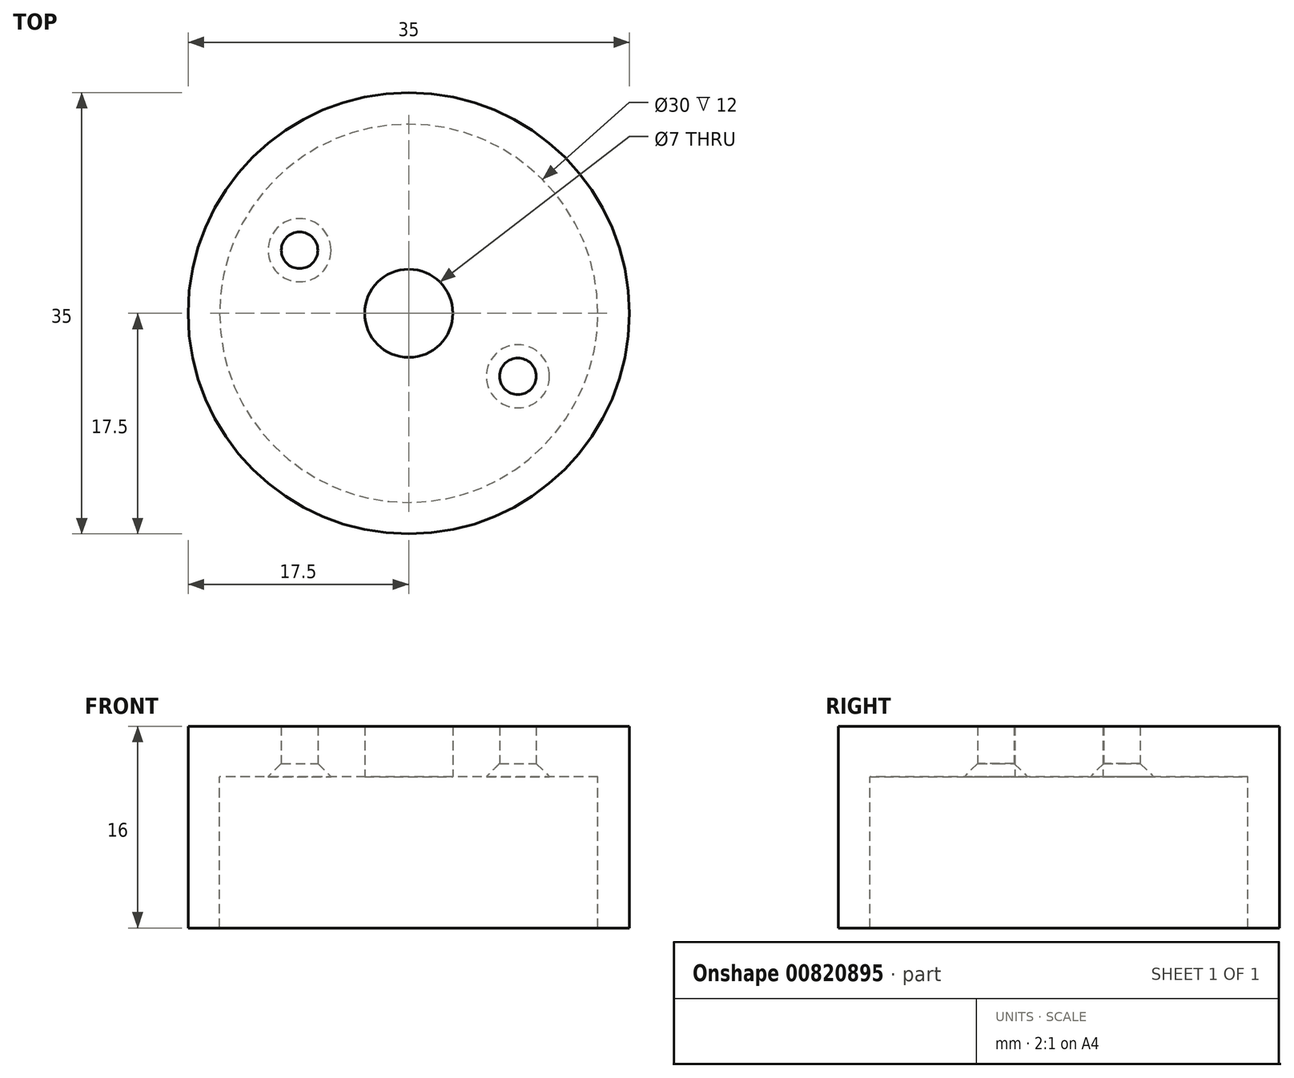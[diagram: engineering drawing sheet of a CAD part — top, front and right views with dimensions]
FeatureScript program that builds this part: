
annotation { "Feature Type Name" : "Feature", "Feature Type Description" : "" }
export const myFeature = defineFeature(function(context is Context, id is Id, definition is map)
    precondition{}
    {
        {
            var Q0;
            Q0=qCreatedBy(makeId("Top.planeOp"),FACE);
            var sketch = newSketch(context, id + "F0", { "sketchPlane" : qUnion([Q0])});
            skCircle(sketch, "E0", {"center": v(0, 0) * mm, "radius": 15 * mm});
            skPoint(sketch, "E1", {"position": v(-8.66, 5) * mm});
            skPoint(sketch, "E2.MirrorP", {"position": v(8.66, -5) * mm});
            skCircle(sketch, "E3", {"center": v(0, 0) * mm, "radius": 17.5 * mm});
            skSolve(sketch);
        }
        {
            var Q0;
            Q0=makeQuery(id+"F0.imprint","IMPRINT",FACE,{"disambiguationData":[TD([[makeQuery(id+"F0.imprint","IMPRINT",EDGE,{"derivedFrom":sQuery(id+"F0.wireOp",EDGE,"2a8dab0b-44af-4e55-a114-fc4188fa64b7.0")}),1.0]])]});
            var Q1;
            Q1=makeQuery(id+"F0.imprint","IMPRINT",FACE,{"disambiguationData":[TD([[makeQuery(id+"F0.imprint","IMPRINT",EDGE,{"derivedFrom":sQuery(id+"F0.wireOp",EDGE,"E0")}),-1.0]])]});
            var Q2;
            Q2=makeQuery(id+"F0.imprint","IMPRINT",FACE,{"disambiguationData":[TD([[makeQuery(id+"F0.imprint","IMPRINT",EDGE,{"derivedFrom":sQuery(id+"F0.wireOp",EDGE,"E0")}),1.0]])]});
            extrude(context, id + "F1", {"entities" : qUnion([Q0, Q1, Q2]), "depth" : 4 * mm, "offsetDistance" : 25 * mm});
        }
        {
            var Q0;
            Q0=makeQuery(id+"F0.imprint","IMPRINT",FACE,{"disambiguationData":[TD([[makeQuery(id+"F0.imprint","IMPRINT",EDGE,{"derivedFrom":sQuery(id+"F0.wireOp",EDGE,"E0")}),-1.0]])]});
            extrude(context, id + "F2", {"entities" : qUnion([Q0]), "operationType" : NewBodyOperationType.ADD, "oppositeDirection" : true, "depth" : 12 * mm, "offsetDistance" : 25 * mm});
        }
        {
            var Q0;
            Q0=sQuery(id+"F0.wireOp",VERTEX,"E2.MirrorP");
            var Q1;
            Q1=sQuery(id+"F0.wireOp",VERTEX,"E1");
            var Q2;
            Q2=makeQuery(id+"F1.opExtrude","SWEPT_BODY",BODY,{"disambiguationData":[OSD([sQuery(id+"F0.wireOp",EDGE,"E3")])]});
            hole(context, id + "F3", {"style" : HoleStyle.C_SINK, "endStyle" : HoleEndStyle.THROUGH, "oppositeDirection" : true, "holeDiameter" : 2.9 * mm, "cSinkDiameter" : 5 * mm, "cSinkAngle" : 90 * degree, "majorDiameter" : 5 * mm, "isTappedThrough" : true, "tappedDepth" : 12 * mm, "tapClearance" : 3, "locations" : qUnion([Q0, Q1]), "scope" : qUnion([Q2])});
        }
        {
            var Q0;
            Q0=sQuery(id+"F0.wireOp",VERTEX,"E0.center");
            var Q1;
            Q1=makeQuery(id+"F1.opExtrude","SWEPT_BODY",BODY,{"disambiguationData":[OSD([sQuery(id+"F0.wireOp",EDGE,"E3")])]});
            hole(context, id + "F4", {"style" : HoleStyle.SIMPLE, "endStyle" : HoleEndStyle.THROUGH, "oppositeDirection" : true, "holeDiameter" : 7 * mm, "majorDiameter" : 5 * mm, "isTappedThrough" : true, "tappedDepth" : 12 * mm, "tapClearance" : 3, "locations" : qUnion([Q0]), "scope" : qUnion([Q1])});
        }
    });
